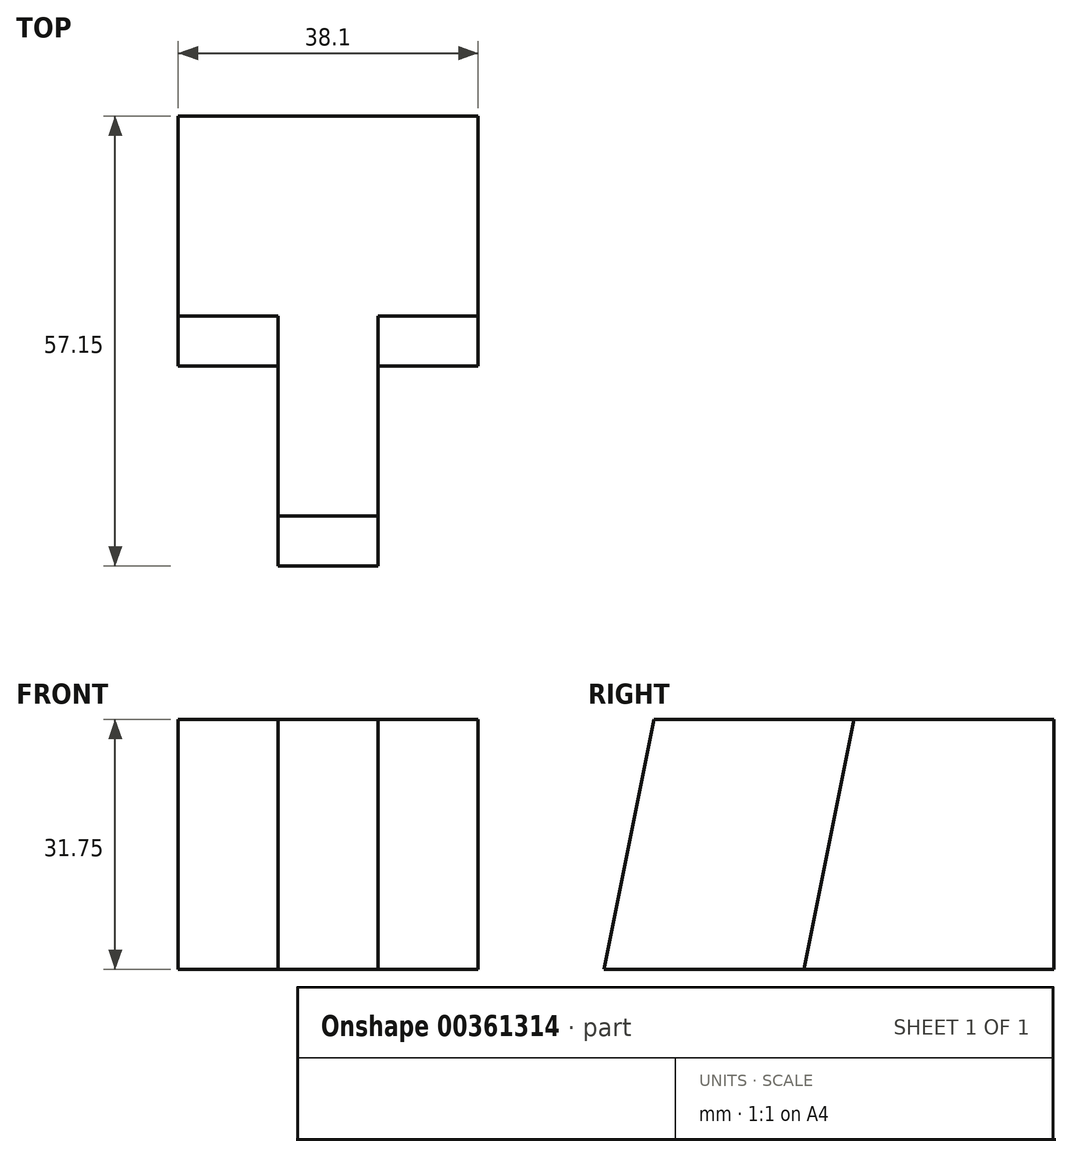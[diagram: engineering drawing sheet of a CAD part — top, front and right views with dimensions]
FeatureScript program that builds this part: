
annotation { "Feature Type Name" : "Feature", "Feature Type Description" : "" }
export const myFeature = defineFeature(function(context is Context, id is Id, definition is map)
    precondition{}
    {
        {
            var Q0;
            Q0=qCreatedBy(makeId("Top.planeOp"),FACE);
            var sketch = newSketch(context, id + "F0", { "sketchPlane" : qUnion([Q0])});
            skLineSegment(sketch, "E0", {"start": v(0, 0) * mm, "end": v(0, 25.4) * mm});
            skLineSegment(sketch, "E1", {"start": v(0, 25.4) * mm, "end": v(-12.7, 25.4) * mm});
            skLineSegment(sketch, "E2", {"start": v(-12.7, 25.4) * mm, "end": v(-12.7, 57.15) * mm});
            skLineSegment(sketch, "E3", {"start": v(-12.7, 57.15) * mm, "end": v(25.4, 57.15) * mm});
            skLineSegment(sketch, "E4", {"start": v(25.4, 57.15) * mm, "end": v(25.4, 25.4) * mm});
            skLineSegment(sketch, "E5", {"start": v(25.4, 25.4) * mm, "end": v(12.7, 25.4) * mm});
            skLineSegment(sketch, "E6", {"start": v(12.7, 25.4) * mm, "end": v(12.7, 0) * mm});
            skLineSegment(sketch, "E7", {"start": v(12.7, 0) * mm, "end": v(0, 0) * mm});
            skSolve(sketch);
        }
        {
            var Q0;
            Q0 = qSketchRegion(id + "F0", true);
            extrude(context, id + "F1", {"entities" : qUnion([Q0]), "depth" : 31.75 * mm});
        }
        {
            var Q0;
            Q0=makeQuery(id+"F1.opExtrude","SWEPT_FACE",FACE,{"disambiguationData":[OSD([sQuery(id+"F0.wireOp",EDGE,"E2")])]});
            var sketch = newSketch(context, id + "F2", { "sketchPlane" : qUnion([Q0])});
            skLineSegment(sketch, "E8", {"start": v(-25.4, 0) * mm, "end": v(-31.75, 31.75) * mm});
            skLineSegment(sketch, "E9", {"start": v(-31.75, 31.75) * mm, "end": v(-25.4, 31.75) * mm});
            skLineSegment(sketch, "E10", {"start": v(-25.4, 31.75) * mm, "end": v(-25.4, 0) * mm});
            skSolve(sketch);
        }
        {
            var Q0;
            Q0 = qSketchRegion(id + "F2", true);
            extrude(context, id + "F3", {"entities" : qUnion([Q0]), "operationType" : NewBodyOperationType.REMOVE, "oppositeDirection" : true, "depth" : 12.7 * mm});
        }
        {
            var Q0;
            Q0=makeQuery(id+"F1.opExtrude","SWEPT_FACE",FACE,{"disambiguationData":[OSD([sQuery(id+"F0.wireOp",EDGE,"E4")])]});
            var sketch = newSketch(context, id + "F4", { "sketchPlane" : qUnion([Q0])});
            skLineSegment(sketch, "E11", {"start": v(25.4, 0) * mm, "end": v(31.75, 31.75) * mm});
            skLineSegment(sketch, "E12", {"start": v(31.75, 31.75) * mm, "end": v(25.4, 31.75) * mm});
            skLineSegment(sketch, "E13", {"start": v(25.4, 31.75) * mm, "end": v(25.4, 0) * mm});
            skSolve(sketch);
        }
        {
            var Q0;
            Q0 = qSketchRegion(id + "F4", true);
            extrude(context, id + "F5", {"entities" : qUnion([Q0]), "operationType" : NewBodyOperationType.REMOVE, "oppositeDirection" : true, "depth" : 12.7 * mm});
        }
        {
            var Q0;
            Q0=makeQuery(id+"F5.boolean.opBoolean","MERGE",FACE,{"derivedFrom":[makeQuery(id+"F1.opExtrude","SWEPT_FACE",FACE,{"disambiguationData":[OSD([sQuery(id+"F0.wireOp",EDGE,"E6")])]}),makeQuery(id+"F5.opExtrude","CAP_FACE",FACE,{"disambiguationData":[OSD([sQuery(id+"F4.wireOp",EDGE,"E11"),sQuery(id+"F4.wireOp",EDGE,"E12"),sQuery(id+"F4.wireOp",EDGE,"E13")])],"isStart":false})]});
            var sketch = newSketch(context, id + "F6", { "sketchPlane" : qUnion([Q0])});
            skLineSegment(sketch, "E14", {"start": v(0, 0) * mm, "end": v(6.35, 31.75) * mm});
            skLineSegment(sketch, "E15", {"start": v(6.35, 31.75) * mm, "end": v(0, 31.75) * mm});
            skLineSegment(sketch, "E16", {"start": v(0, 31.75) * mm, "end": v(0, 0) * mm});
            skSolve(sketch);
        }
        {
            var Q0;
            Q0 = qSketchRegion(id + "F6", true);
            extrude(context, id + "F7", {"entities" : qUnion([Q0]), "operationType" : NewBodyOperationType.REMOVE, "oppositeDirection" : true, "depth" : 12.7 * mm});
        }
    });
